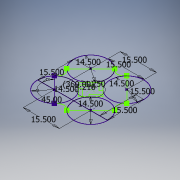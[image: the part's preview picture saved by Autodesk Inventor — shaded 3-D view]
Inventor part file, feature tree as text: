
AUTODESK INVENTOR PART (.ipt)
format: ipt  version: 2017 (Build 210142000, 142)  size: 115,712 bytes
history: native  units: in
note: dims shown in document units (in); Inventor stores cm internally (conversion verified against a paired STEP export)
features: sketch x1
ambient origin geometry x8: Origin, YZ Plane, XZ Plane, XY Plane, X Axis, Y Axis, Z Axis, Center Point
feature tree (1):
  sketch  "Sketch1"  dims[d0=14.5in d1=15.5in d2=14.5in d3=45.0deg d4=15.5in d5=14.5in d6=14.5in d7=15.5in d8=15.5in d11=15.5in d12=15.5in d13=4.21in d14=1.25in d15=1.5748in d17=360.0deg]
